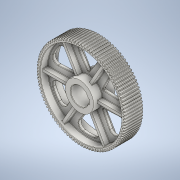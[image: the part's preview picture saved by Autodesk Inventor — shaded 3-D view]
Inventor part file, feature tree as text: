
AUTODESK INVENTOR PART (.ipt)
format: ipt  version: 2020 (Build 240168000, 168)  size: 1,822,208 bytes
history: native  units: mm (DEFAULTED — no unit token found)
features: extrude x8, sketch x8, plane x6, chamfer x4, pattern_circular x3, other x2, fillet x2, loft x1, mirror x1
ambient origin geometry x8: Origin, YZ Plane, XZ Plane, XY Plane, X Axis, Y Axis, Z Axis, Center Point
bodies: Solid1 (feature_tree)
feature tree (35):
  extrude  "Extrusion1"  Depth=125.0mm TaperAngle=0.0deg
  plane  "Work Plane2"
  plane  "Work Plane8"
  plane  "Work Plane9"
  other  "正齿轮"
  extrude  "拉伸2"  Depth=10.0mm TaperAngle=0.0deg
  extrude  "拉伸3"  Depth=0.320571mm TaperAngle=0.0deg
  extrude  "拉伸4"  TaperAngle=0.0deg  [1 undecoded]
  plane  "工作平面11"
  sketch  "草图9"  dims[d47=0.0mm d48=0.0mm d50=192.0mm]
  plane  "工作平面12"
  loft  "放样1"
  extrude  "拉伸5"  Depth=192.0mm
  pattern_circular  "环形阵列1"  Count=12  [1 undecoded]
  extrude  "拉伸6"  Depth=3.0mm
  extrude  "拉伸7"  Depth=18.0mm
  pattern_circular  "环形阵列2"  [2 undecoded]
  chamfer  "倒角2"  Distance=552.0mm
  chamfer  "倒角3"  Distance=9.5mm
  chamfer  "倒角4"  Distance=96.0mm
  chamfer  "倒角5"  Distance=18.0mm
  extrude  "拉伸8"  Depth=3.0mm
  pattern_circular  "环形阵列3"  [2 undecoded]
  fillet  "圆角1"  Radius=21.6mm
  plane  "工作平面13"
  mirror  "镜像1"
  fillet  "圆角2"  Radius=108.0mm
  sketch  "Sketch1"  dims[d0=600.0mm d1=125.0mm d2=0.0mm]
  sketch  "Sketch2"  dims[d3=588.0mm d4=10.0mm d5=0.0mm]
  other  "Srf1"
  sketch  "草图6"  dims[d16=357.0mm d17=0.0mm d34=0.320571mm]
  sketch  "草图7"  dims[d39=0.0mm d41=0.0mm]
  sketch  "草图8"  dims[d43=357.0mm d46=357.0mm]
  sketch  "草图10"  dims[d51=9.5mm d52=134.5mm d53=0.0mm d54=0.0mm d55=120.0mm]
  sketch  "草图11"  dims[d56=32.0mm d57=7.0mm d58=18.0mm d59=9.5mm d60=0.0mm d61=552.0mm d62=9.5mm d63=0.0mm d64=96.0mm d65=18.0mm d66=89.0mm d67=62.5mm d68=21.6mm d69=108.0mm d70=276.0mm d71=18.0mm d72=89.0mm d73=21.6mm d74=86.4mm d75=0.0mm d76=90.0deg d77=0.0mm d78=90.0deg d79=9.5mm d80=0.0mm d81=60.0mm d82=360.0deg d84=9.5mm d85=0.0mm d86=516.0mm d87=228.0mm d88=68.0mm d89=68.0mm d90=6.0mm d91=6.0mm d92=9.5mm d93=0.0mm d94=60.0mm d95=360.0deg d100=3.0mm d101=2.0mm d102=45.0deg d103=3.0mm d104=2.0mm d105=45.0deg d106=3.0mm d107=2.0mm d108=45.0deg d109=3.0mm d110=2.0mm d111=45.0deg d112=3.0mm d113=10.0mm d114=0.0mm d115=60.0mm d116=360.0deg d120=3.0mm]
note: 6 required parameter values undecoded (feature->parameter linkage not recoverable at this tier; creation-order binding heuristic only, values carry confidence <= 0.55)
